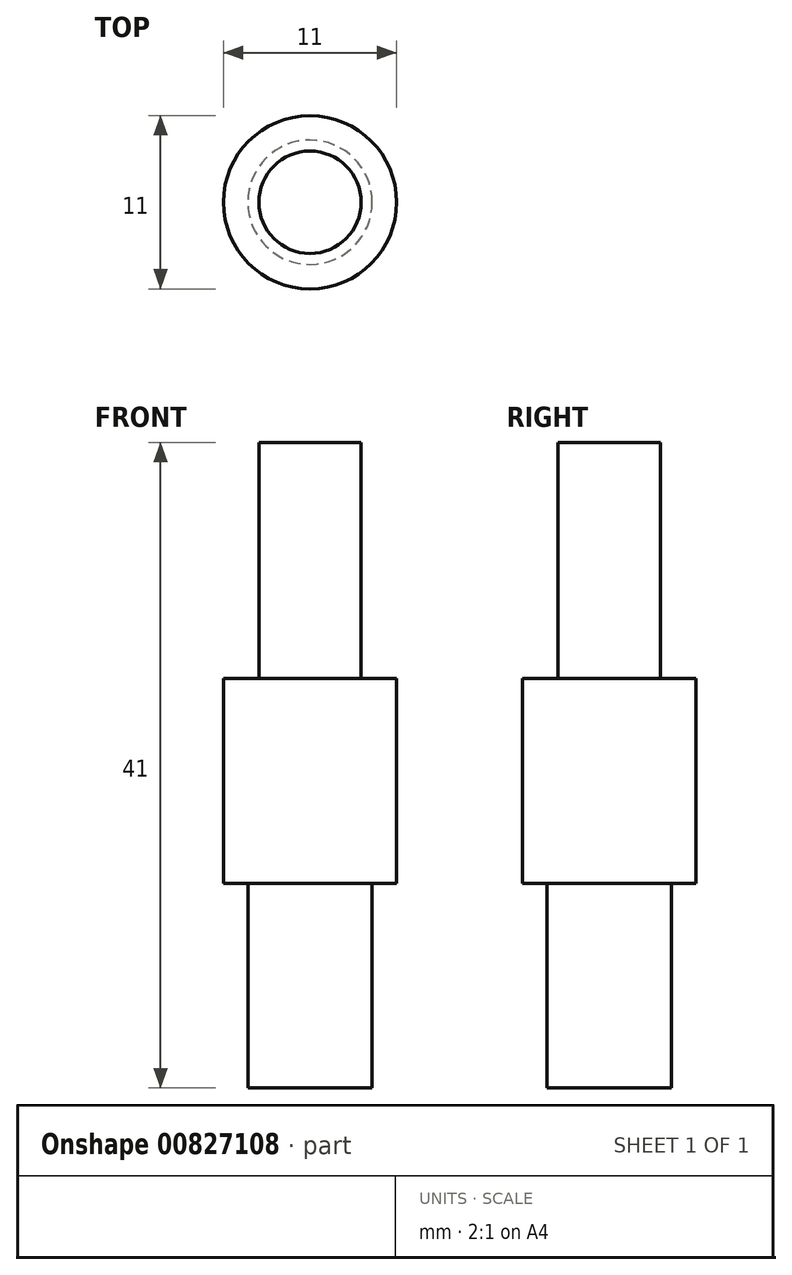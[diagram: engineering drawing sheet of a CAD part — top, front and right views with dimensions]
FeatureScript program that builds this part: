
annotation { "Feature Type Name" : "Feature", "Feature Type Description" : "" }
export const myFeature = defineFeature(function(context is Context, id is Id, definition is map)
    precondition{}
    {
        {
            var Q0;
            Q0=qCreatedBy(makeId("Top.planeOp"),FACE);
            var sketch = newSketch(context, id + "F0", { "sketchPlane" : qUnion([Q0])});
            skCircle(sketch, "E0", {"center": v(0, 0) * mm, "radius": 5.5 * mm});
            skSolve(sketch);
        }
        {
            var Q0;
            Q0=makeQuery(id+"F0.imprint","IMPRINT",FACE,{"disambiguationData":[TD([[makeQuery(id+"F0.imprint","IMPRINT",EDGE,{"derivedFrom":sQuery(id+"F0.wireOp",EDGE,"E0")}),1.0]])]});
            extrude(context, id + "F1", {"entities" : qUnion([Q0]), "depth" : (13) * mm, "offsetDistance" : 25 * mm});
        }
        {
            var Q0;
            Q0=makeQuery(id+"F1.opExtrude","CAP_FACE",FACE,{"disambiguationData":[OSD([sQuery(id+"F0.wireOp",EDGE,"E0")])],"isStart":false});
            var sketch = newSketch(context, id + "F2", { "sketchPlane" : qUnion([Q0])});
            skCircle(sketch, "E1", {"center": v(0, 0) * mm, "radius": 3.25 * mm});
            skSolve(sketch);
        }
        {
            var Q0;
            Q0=makeQuery(id+"F2.imprint","IMPRINT",FACE,{"disambiguationData":[TD([[makeQuery(id+"F2.imprint","IMPRINT",EDGE,{"derivedFrom":sQuery(id+"F2.wireOp",EDGE,"E1")}),1.0]])]});
            extrude(context, id + "F3", {"entities" : qUnion([Q0]), "operationType" : NewBodyOperationType.ADD, "depth" : (15) * mm, "offsetDistance" : 25 * mm});
        }
        {
            var Q0;
            Q0=makeQuery(id+"F1.opExtrude","CAP_FACE",FACE,{"disambiguationData":[OSD([sQuery(id+"F0.wireOp",EDGE,"E0")])],"isStart":true});
            var sketch = newSketch(context, id + "F4", { "sketchPlane" : qUnion([Q0])});
            skCircle(sketch, "E2", {"center": v(0, 0) * mm, "radius": 3.95 * mm});
            skSolve(sketch);
        }
        {
            var Q0;
            Q0=makeQuery(id+"F4.imprint","IMPRINT",FACE,{"disambiguationData":[TD([[makeQuery(id+"F4.imprint","IMPRINT",EDGE,{"derivedFrom":sQuery(id+"F4.wireOp",EDGE,"E2")}),1.0]])]});
            extrude(context, id + "F5", {"entities" : qUnion([Q0]), "operationType" : NewBodyOperationType.ADD, "depth" : (13) * mm, "offsetDistance" : 25 * mm});
        }
    });
